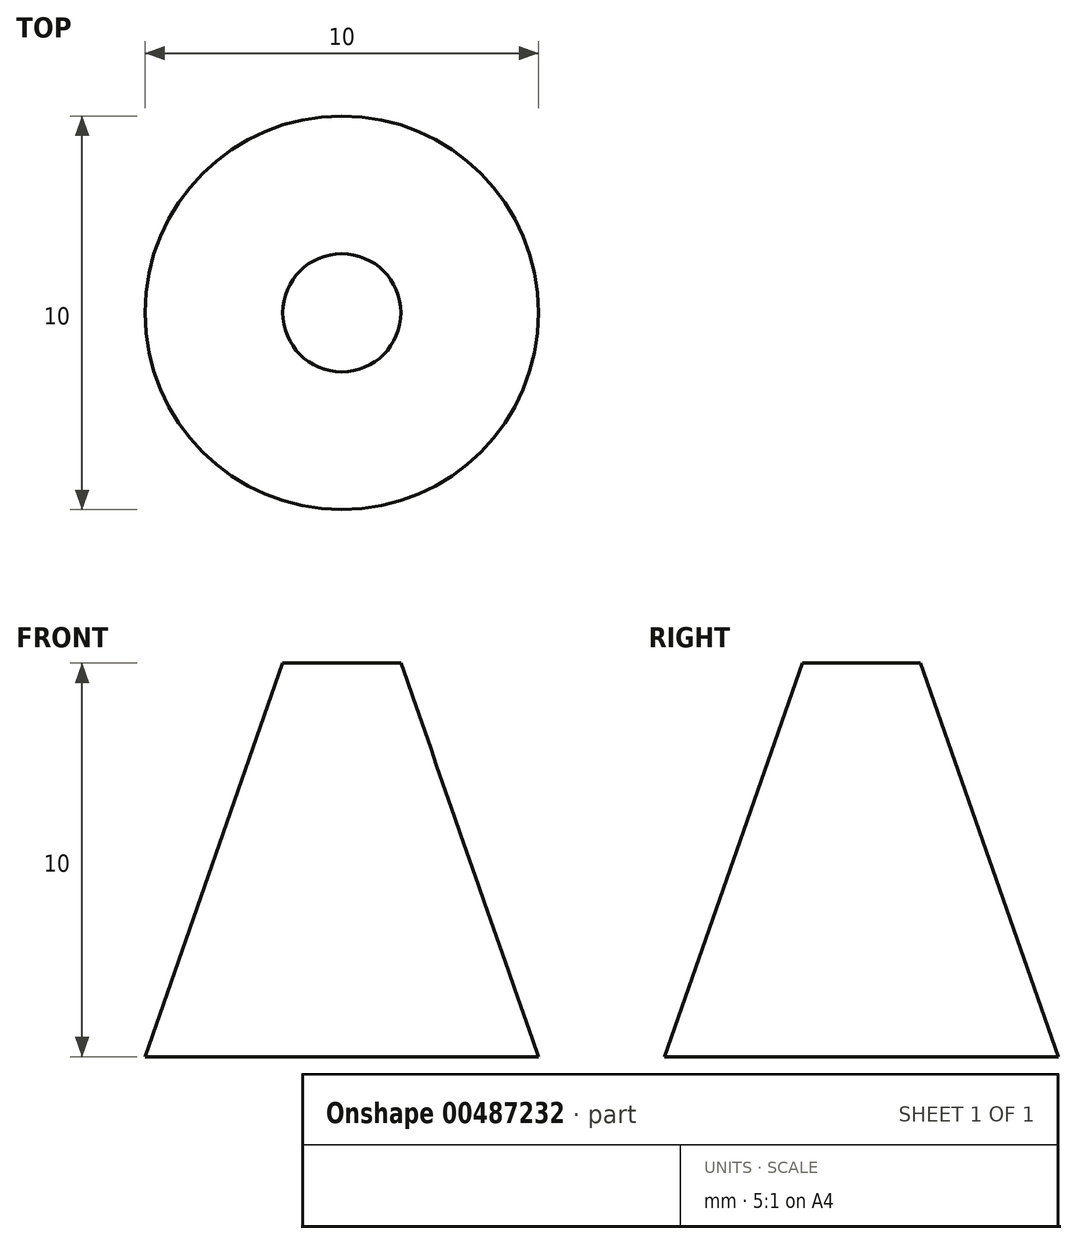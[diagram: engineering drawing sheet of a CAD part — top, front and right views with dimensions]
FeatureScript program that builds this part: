
annotation { "Feature Type Name" : "Feature", "Feature Type Description" : "" }
export const myFeature = defineFeature(function(context is Context, id is Id, definition is map)
    precondition{}
    {
        {
            var Q0;
            Q0=qCreatedBy(makeId("Front.planeOp"),FACE);
            var sketch = newSketch(context, id + "F0", { "sketchPlane" : qUnion([Q0])});
            skLineSegment(sketch, "E0", {"start": v(0, 0) * mm, "end": v(-5, 0) * mm});
            skLineSegment(sketch, "E1", {"start": v(-5, 0) * mm, "end": v(-1.5, 10) * mm});
            skLineSegment(sketch, "E2", {"start": v(-1.5, 10) * mm, "end": v(0, 10) * mm});
            skLineSegment(sketch, "E3", {"start": v(0, 10) * mm, "end": v(0, 0) * mm});
            skSolve(sketch);
        }
        {
            var Q0;
            Q0=qCreatedBy(makeId("Front.planeOp"),FACE);
            var sketch = newSketch(context, id + "F1", { "sketchPlane" : qUnion([Q0])});
            skLineSegment(sketch, "E4", {"start": v(0, 11.04) * mm, "end": v(0, -2.07) * mm, "construction": true});
            skSolve(sketch);
        }
        {
            var Q0;
            Q0=makeQuery(id+"F0.imprint","IMPRINT",FACE,{"disambiguationData":[TD([[makeQuery(id+"F0.imprint","IMPRINT",EDGE,{"derivedFrom":sQuery(id+"F0.wireOp",EDGE,"E0")}),-1.0]])]});
            var Q1;
            Q1=sQuery(id+"F1.wireOp",EDGE,"E4");
            revolve(context, id + "F2", {"entities" : qUnion([Q0]), "axis" : qUnion([Q1]), "revolveType" : RevolveType.FULL});
        }
    });
